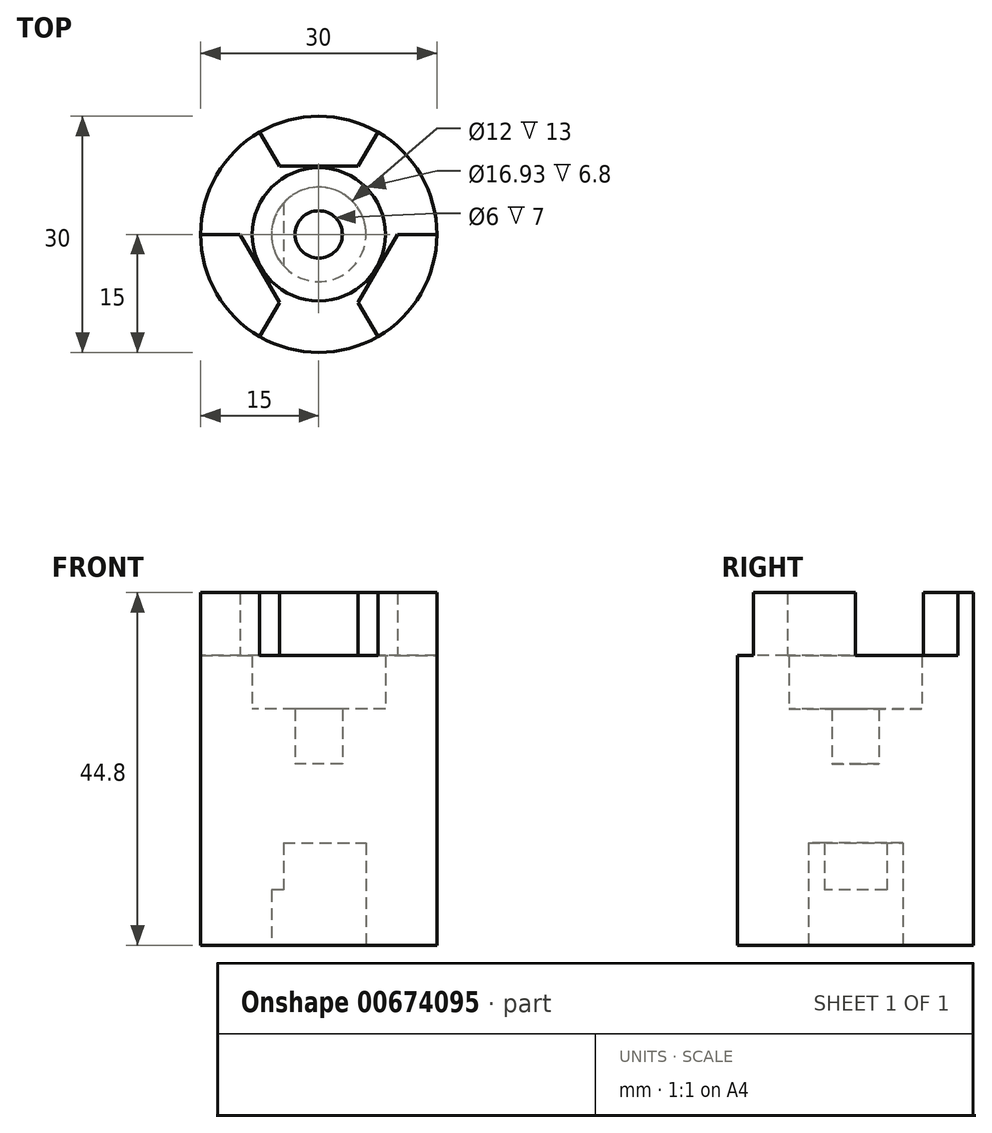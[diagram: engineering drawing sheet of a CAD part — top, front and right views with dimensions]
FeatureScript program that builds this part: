
annotation { "Feature Type Name" : "Feature", "Feature Type Description" : "" }
export const myFeature = defineFeature(function(context is Context, id is Id, definition is map)
    precondition{}
    {
        {
            var Q0;
            Q0=qCreatedBy(makeId("Top.planeOp"),FACE);
            var sketch = newSketch(context, id + "F0", { "sketchPlane" : qUnion([Q0])});
            skCircle(sketch, "E0", {"center": v(0, 0) * mm, "radius": 6 * mm});
            skCircle(sketch, "E1", {"center": v(0, 0) * mm, "radius": 15 * mm});
            skLineSegment(sketch, "E2", {"start": v(-4.5, 3.97) * mm, "end": v(-4.5, -3.97) * mm});
            skSolve(sketch);
        }
        {
            var Q0;
            Q0=makeQuery(id+"F0.imprint","IMPRINT",FACE,{"disambiguationData":[TD([[makeQuery(id+"F0.imprint","IMPRINT",EDGE,{"derivedFrom":sQuery(id+"F0.wireOp",EDGE,"E0")}),-1.0]])]});
            extrude(context, id + "F1", {"entities" : qUnion([Q0]), "depth" : 7 * mm, "offsetDistance" : 25 * mm});
        }
        {
            var Q0;
            Q0=makeQuery(id+"F1.opExtrude","CAP_FACE",FACE,{"disambiguationData":[OSD([sQuery(id+"F0.wireOp",EDGE,"E0"),sQuery(id+"F0.wireOp",EDGE,"E1")])],"isStart":false});
            var sketch = newSketch(context, id + "F2", { "sketchPlane" : qUnion([Q0])});
            skCircle(sketch, "E3", {"center": v(0, 0) * mm, "radius": 6 * mm});
            skCircle(sketch, "E4", {"center": v(0, 0) * mm, "radius": 15 * mm});
            skLineSegment(sketch, "E5", {"start": v(-4.5, 3.97) * mm, "end": v(-4.5, -3.97) * mm});
            skSolve(sketch);
        }
        {
            var Q0;
            {var subQ0=sQuery(id+"F2.wireOp",EDGE,"E5");Q0=makeQuery(id+"F2.imprint","IMPRINT",FACE,{"disambiguationData":[TD([[makeQuery(id+"F2.imprint","IMPRINT",EDGE,{"derivedFrom":subQ0}),-1.0]])]});}
            var Q1;
            Q1=makeQuery(id+"F2.imprint","IMPRINT",FACE,{"disambiguationData":[TD([[makeQuery(id+"F2.imprint","IMPRINT",EDGE,{"derivedFrom":sQuery(id+"F2.wireOp",EDGE,"E4")}),1.0]])]});
            extrude(context, id + "F3", {"entities" : qUnion([Q0, Q1]), "operationType" : NewBodyOperationType.ADD, "depth" : 6 * mm, "offsetDistance" : 25 * mm});
        }
        {
            var Q0;
            Q0=makeQuery(id+"F3.opExtrude","CAP_FACE",FACE,{"disambiguationData":[OSD([sQuery(id+"F2.wireOp",EDGE,"E3"),sQuery(id+"F2.wireOp",EDGE,"E4"),sQuery(id+"F2.wireOp",EDGE,"E5")])],"isStart":false});
            var Q1;
            Q1=makeQuery(id+"F3.opExtrude","CAP_FACE",FACE,{"disambiguationData":[OSD([sQuery(id+"F2.wireOp",EDGE,"E3"),sQuery(id+"F2.wireOp",EDGE,"E4"),sQuery(id+"F2.wireOp",EDGE,"E5")])],"isStart":false});
            var sketch = newSketch(context, id + "F4", { "sketchPlane" : qUnion([Q0, Q1])});
            skCircle(sketch, "E6", {"center": v(0, 0) * mm, "radius": 15 * mm});
            skSolve(sketch);
        }
        {
            var Q0;
            Q0=makeQuery(id+"F4.imprint","IMPRINT",FACE,{"disambiguationData":[TD([[makeQuery(id+"F4.imprint","IMPRINT",EDGE,{"derivedFrom":sQuery(id+"F4.wireOp",EDGE,"E6")}),1.0]])]});
            var Q1;
            Q1=makeQuery(id+"F4.imprint","IMPRINT",FACE,{"disambiguationData":[TD([[makeQuery(id+"F4.imprint","IMPRINT",EDGE,{"derivedFrom":makeQuery(id+"F3.opExtrude","CAP_EDGE",EDGE,{"disambiguationData":[OSD([sQuery(id+"F2.wireOp",EDGE,"E3")])],"isStart":false})}),1.0]])]});
            extrude(context, id + "F5", {"entities" : qUnion([Q0, Q1]), "operationType" : NewBodyOperationType.ADD, "depth" : 10 * mm, "offsetDistance" : 25 * mm});
        }
        {
            var Q0;
            Q0=makeQuery(id+"F5.opExtrude","CAP_FACE",FACE,{"disambiguationData":[OSD([sQuery(id+"F4.wireOp",EDGE,"E6")])],"isStart":false});
            var sketch = newSketch(context, id + "F6", { "sketchPlane" : qUnion([Q0])});
            skCircle(sketch, "E7", {"center": v(0, 0) * mm, "radius": 15 * mm});
            skLineSegment(sketch, "E8", {"start": v(15, 0) * mm, "end": v(10, 0) * mm});
            skLineSegment(sketch, "E9", {"start": v(10, 0) * mm, "end": v(5, -8.66) * mm});
            skLineSegment(sketch, "E10", {"start": v(5, -8.66) * mm, "end": v(7.5, -13) * mm});
            skLineSegment(sketch, "E11.1.0", {"start": v(-5, 8.66) * mm, "end": v(5, 8.66) * mm});
            skLineSegment(sketch, "E11.1.1", {"start": v(-7.5, 13) * mm, "end": v(-5, 8.66) * mm});
            skLineSegment(sketch, "E11.1.2", {"start": v(5, 8.66) * mm, "end": v(7.5, 13) * mm});
            skLineSegment(sketch, "E11.2.0", {"start": v(-5, -8.66) * mm, "end": v(-10, 0) * mm});
            skLineSegment(sketch, "E11.2.1", {"start": v(-7.5, -13) * mm, "end": v(-5, -8.66) * mm});
            skLineSegment(sketch, "E11.2.2", {"start": v(-10, 0) * mm, "end": v(-15, 0) * mm});
            skCircle(sketch, "E12", {"center": v(0, 0) * mm, "radius": 3 * mm});
            skCircle(sketch, "E13", {"center": v(0, 0) * mm, "radius": 8.47 * mm});
            skSolve(sketch);
        }
        {
            var Q0;
            {var subQ0=sQuery(id+"F6.wireOp",EDGE,"E11.2.0");Q0=makeQuery(id+"F6.imprint","IMPRINT",FACE,{"disambiguationData":[TD([[makeQuery(id+"F6.imprint","IMPRINT",EDGE,{"derivedFrom":subQ0}),1.0]])]});}
            var Q1;
            {var subQ0=sQuery(id+"F6.wireOp",EDGE,"E9");Q1=makeQuery(id+"F6.imprint","IMPRINT",FACE,{"disambiguationData":[TD([[makeQuery(id+"F6.imprint","IMPRINT",EDGE,{"derivedFrom":subQ0}),1.0]])]});}
            var Q2;
            {var subQ0=sQuery(id+"F6.wireOp",EDGE,"E11.1.0");Q2=makeQuery(id+"F6.imprint","IMPRINT",FACE,{"disambiguationData":[TD([[makeQuery(id+"F6.imprint","IMPRINT",EDGE,{"derivedFrom":subQ0}),1.0]])]});}
            var Q3;
            Q3=makeQuery(id+"F6.imprint","IMPRINT",FACE,{"disambiguationData":[TD([[makeQuery(id+"F6.imprint","IMPRINT",EDGE,{"derivedFrom":sQuery(id+"F6.wireOp",EDGE,"bc1c6984-8711-4058-a226-701a726c2491.0")}),-1.0]])]});
            var Q4;
            Q4=makeQuery(id+"F6.imprint","IMPRINT",FACE,{"disambiguationData":[TD([[makeQuery(id+"F6.imprint","IMPRINT",EDGE,{"derivedFrom":sQuery(id+"F6.wireOp",EDGE,"bc1c6984-8711-4058-a226-701a726c2491.0")}),1.0]])]});
            var Q5;
            {var subQ9=sQuery(id+"F6.wireOp",EDGE,"E9");Q5=makeQuery(id+"F6.imprint","IMPRINT",FACE,{"disambiguationData":[TD([[makeQuery(id+"F6.imprint","IMPRINT",EDGE,{"derivedFrom":subQ9}),-1.0]])]});}
            var Q6;
            Q6=makeQuery(id+"F6.imprint","IMPRINT",FACE,{"disambiguationData":[TD([[makeQuery(id+"F6.imprint","IMPRINT",EDGE,{"derivedFrom":sQuery(id+"F6.wireOp",EDGE,"E12")}),-1.0]])]});
            extrude(context, id + "F7", {"entities" : qUnion([Q0, Q1, Q2, Q3, Q4, Q5, Q6]), "operationType" : NewBodyOperationType.ADD, "depth" : (9 - 2) * mm, "offsetDistance" : 25 * mm});
        }
        {
            var Q0;
            {var subQ0=sQuery(id+"F6.wireOp",EDGE,"E11.1.0");Q0=makeQuery(id+"F6.imprint","IMPRINT",FACE,{"disambiguationData":[TD([[makeQuery(id+"F6.imprint","IMPRINT",EDGE,{"derivedFrom":subQ0}),1.0]])]});}
            var Q1;
            {var subQ0=sQuery(id+"F6.wireOp",EDGE,"E9");Q1=makeQuery(id+"F6.imprint","IMPRINT",FACE,{"disambiguationData":[TD([[makeQuery(id+"F6.imprint","IMPRINT",EDGE,{"derivedFrom":subQ0}),1.0]])]});}
            var Q2;
            {var subQ0=sQuery(id+"F6.wireOp",EDGE,"E11.2.0");Q2=makeQuery(id+"F6.imprint","IMPRINT",FACE,{"disambiguationData":[TD([[makeQuery(id+"F6.imprint","IMPRINT",EDGE,{"derivedFrom":subQ0}),1.0]])]});}
            var Q3;
            {var subQ9=sQuery(id+"F6.wireOp",EDGE,"E9");Q3=makeQuery(id+"F6.imprint","IMPRINT",FACE,{"disambiguationData":[TD([[makeQuery(id+"F6.imprint","IMPRINT",EDGE,{"derivedFrom":subQ9}),-1.0]])]});}
            extrude(context, id + "F8", {"entities" : qUnion([Q0, Q1, Q2, Q3]), "operationType" : NewBodyOperationType.ADD, "depth" : 13.8 * mm, "offsetDistance" : 25 * mm});
        }
        {
            var Q0;
            {var subQ0=sQuery(id+"F6.wireOp",EDGE,"E11.2.0");Q0=makeQuery(id+"F6.imprint","IMPRINT",FACE,{"disambiguationData":[TD([[makeQuery(id+"F6.imprint","IMPRINT",EDGE,{"derivedFrom":subQ0}),1.0]])]});}
            var Q1;
            {var subQ0=sQuery(id+"F6.wireOp",EDGE,"E11.1.0");Q1=makeQuery(id+"F6.imprint","IMPRINT",FACE,{"disambiguationData":[TD([[makeQuery(id+"F6.imprint","IMPRINT",EDGE,{"derivedFrom":subQ0}),1.0]])]});}
            var Q2;
            {var subQ0=sQuery(id+"F6.wireOp",EDGE,"E9");Q2=makeQuery(id+"F6.imprint","IMPRINT",FACE,{"disambiguationData":[TD([[makeQuery(id+"F6.imprint","IMPRINT",EDGE,{"derivedFrom":subQ0}),1.0]])]});}
            extrude(context, id + "F9", {"entities" : qUnion([Q0, Q1, Q2]), "operationType" : NewBodyOperationType.ADD, "depth" : (13.8 + 8) * mm, "offsetDistance" : 25 * mm});
        }
    });
